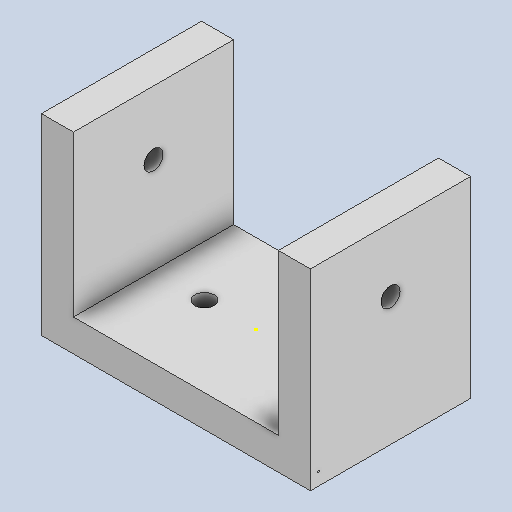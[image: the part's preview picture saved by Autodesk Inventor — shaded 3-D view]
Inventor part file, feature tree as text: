
AUTODESK INVENTOR PART (.ipt)
format: ipt  version: 2023 (Build 270158000, 158)  size: 137,216 bytes
history: native  units: in
note: dims shown in document units (in); Inventor stores cm internally (conversion verified against a paired STEP export)
features: sketch x8, extrude x6
ambient origin geometry x8: Origin, YZ Plane, XZ Plane, XY Plane, X Axis, Y Axis, Z Axis, Center Point
bodies: Solid1 (feature_tree)
feature tree (14):
  extrude  "Extrusion1"  Depth=0.9843in
  sketch  "Sketch5"  dims[d2=0.1969in d3=0.0in d11=0.0118in]
  extrude  "Extrusion5"  Depth=0.1969in
  extrude  "Extrusion6"  Depth=0.1969in
  extrude  "Extrusion7"  Depth=0.1969in
  extrude  "Extrusion8"  Depth=0.9843in
  sketch  "Sketch11"  dims[d24=0.1181in]
  extrude  "Extrusion9"  Depth=0.1181in
  sketch  "Sketch1"  dims[d0=1.6535in d1=0.9843in]
  sketch  "Sketch6"  dims[d12=0.3937in d13=0.0in d14=0.1969in]
  sketch  "Sketch8"  dims[d15=0.9843in d16=0.0in d17=0.1969in]
  sketch  "Sketch9"  dims[d18=0.9843in d19=0.0in d20=0.1181in]
  sketch  "Sketch10"  dims[d21=3.937in d22=0.0in d23=0.1181in]
  sketch  "Sketch12"  dims[d25=0.3937in d26=0.0in]
